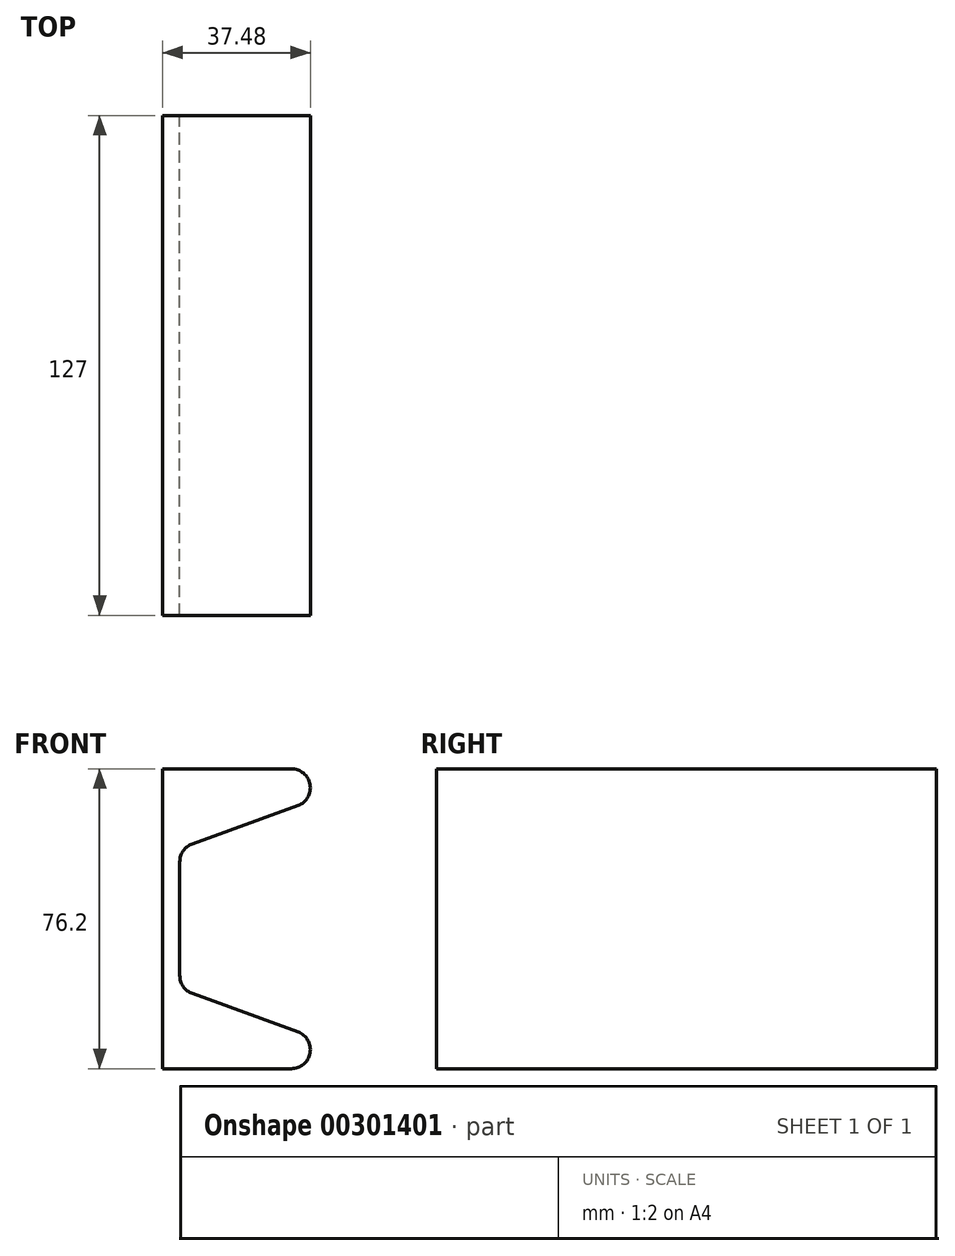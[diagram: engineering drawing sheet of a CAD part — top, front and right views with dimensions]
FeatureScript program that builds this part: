
annotation { "Feature Type Name" : "Feature", "Feature Type Description" : "" }
export const myFeature = defineFeature(function(context is Context, id is Id, definition is map)
    precondition{}
    {
        {
            var Q0;
            Q0=qCreatedBy(makeId("Front.planeOp"),FACE);
            var sketch = newSketch(context, id + "F0", { "sketchPlane" : qUnion([Q0])});
            skLineSegment(sketch, "E0", {"start": v(0, 0) * mm, "end": v(32.65, 0) * mm});
            skLineSegment(sketch, "E1", {"start": v(34.3, 9.36) * mm, "end": v(7.51, 19.08) * mm});
            skLineSegment(sketch, "E2", {"start": v(4.32, 23.64) * mm, "end": v(4.32, 38.1) * mm});
            skLineSegment(sketch, "E3", {"start": v(0, 0) * mm, "end": v(0, 38.1) * mm});
            skPoint(sketch, "E4.visualSharp", {"position": v(60.1, 0) * mm});
            skArc(sketch, "E4.filletArc", {"start": v(32.65, 0) * mm, "mid": v(37.4, 4) * mm, "end": v(34.3, 9.36) * mm});
            skArc(sketch, "E5.MirrorCS", {"start": v(32.65, 76.2) * mm, "mid": v(37.4, 72.2) * mm, "end": v(34.3, 66.84) * mm});
            skLineSegment(sketch, "E6.MirrorCS", {"start": v(0, 76.2) * mm, "end": v(0, 38.1) * mm});
            skLineSegment(sketch, "E7.MirrorCS", {"start": v(0, 76.2) * mm, "end": v(32.65, 76.2) * mm});
            skLineSegment(sketch, "E8.MirrorCS", {"start": v(34.3, 66.84) * mm, "end": v(7.51, 57.12) * mm});
            skLineSegment(sketch, "E9.MirrorCS", {"start": v(4.32, 52.56) * mm, "end": v(4.32, 38.1) * mm});
            skPoint(sketch, "E10.visualSharp", {"position": v(4.32, 20.24) * mm});
            skArc(sketch, "E10.filletArc", {"start": v(4.32, 23.64) * mm, "mid": v(5.2, 20.86) * mm, "end": v(7.51, 19.08) * mm});
            skPoint(sketch, "E11.visualSharp", {"position": v(4.32, 55.96) * mm});
            skArc(sketch, "E11.filletArc", {"start": v(7.51, 57.12) * mm, "mid": v(5.2, 55.34) * mm, "end": v(4.32, 52.56) * mm});
            skSolve(sketch);
        }
        {
            var Q0;
            Q0=makeQuery(id+"F0.imprint","IMPRINT",FACE,{"disambiguationData":[TD([[makeQuery(id+"F0.imprint","IMPRINT",EDGE,{"derivedFrom":sQuery(id+"F0.wireOp",EDGE,"E0")}),1.0]])]});
            extrude(context, id + "F1", {"entities" : qUnion([Q0]), "depth" : 127 * mm});
        }
    });
